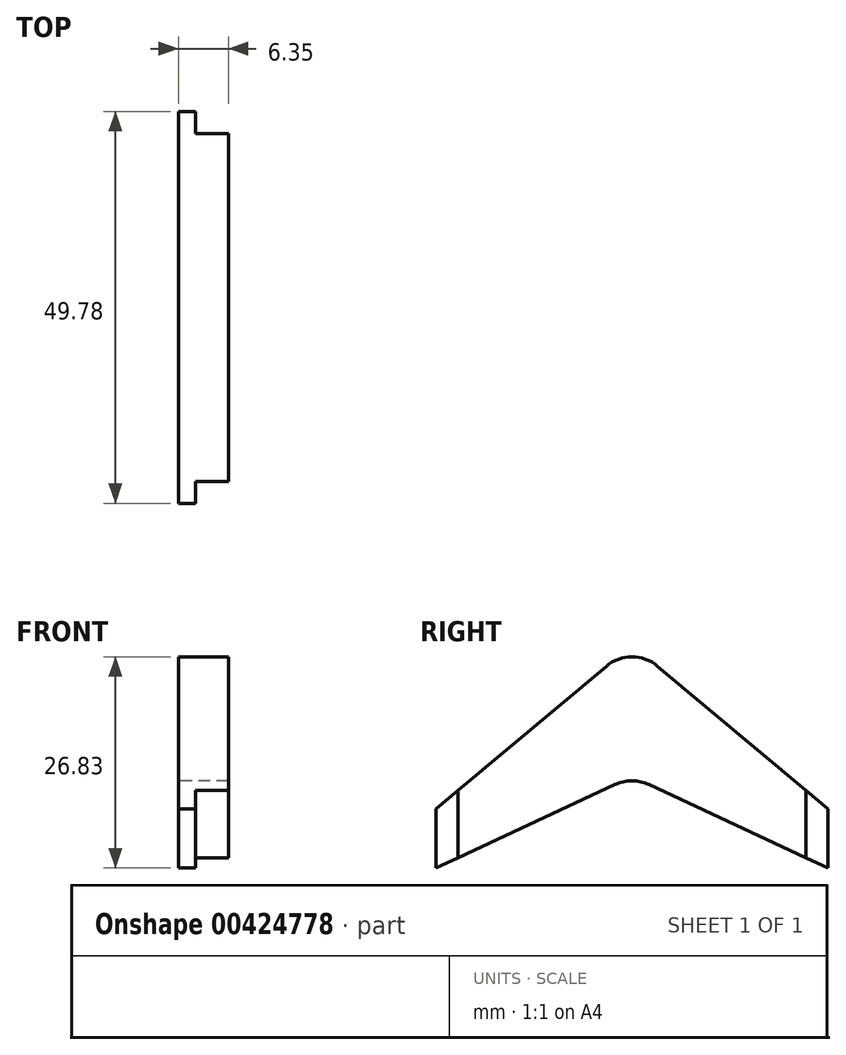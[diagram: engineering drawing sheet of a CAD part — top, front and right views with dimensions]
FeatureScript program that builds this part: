
annotation { "Feature Type Name" : "Feature", "Feature Type Description" : "" }
export const myFeature = defineFeature(function(context is Context, id is Id, definition is map)
    precondition{}
    {
        {
            var Q0;
            Q0=qCreatedBy(makeId("Right.planeOp"),FACE);
            var sketch = newSketch(context, id + "F0", { "sketchPlane" : qUnion([Q0])});
            skArc(sketch, "E0", {"start": v(3.27, 14.56) * mm, "mid": v(1.74, 15.44) * mm, "end": v(0, 15.75) * mm});
            skLineSegment(sketch, "E1", {"start": v(3.27, 14.56) * mm, "end": v(24.9, -3.59) * mm});
            skLineSegment(sketch, "E2", {"start": v(24.9, -3.59) * mm, "end": v(24.9, -11.08) * mm});
            skLineSegment(sketch, "E3", {"start": v(24.9, -11.08) * mm, "end": v(2.15, -0.48) * mm});
            skArc(sketch, "E4", {"start": v(2.15, -0.48) * mm, "mid": v(1.1, -0.12) * mm, "end": v(0, 0) * mm});
            skArc(sketch, "E5.MirrorCS", {"start": v(-2.15, -0.48) * mm, "mid": v(-1.1, -0.12) * mm, "end": v(0, 0) * mm});
            skLineSegment(sketch, "E6.MirrorCS", {"start": v(-24.9, -11.08) * mm, "end": v(-2.15, -0.48) * mm});
            skLineSegment(sketch, "E7.MirrorCS", {"start": v(-24.9, -3.59) * mm, "end": v(-24.9, -11.08) * mm});
            skLineSegment(sketch, "E8.MirrorCS", {"start": v(-3.27, 14.56) * mm, "end": v(-24.9, -3.59) * mm});
            skArc(sketch, "E9.MirrorCS", {"start": v(-3.27, 14.56) * mm, "mid": v(-1.74, 15.44) * mm, "end": v(0, 15.75) * mm});
            skSolve(sketch);
        }
        {
            var Q0;
            Q0=makeQuery(id+"F0.imprint","IMPRINT",FACE,{"disambiguationData":[TD([[makeQuery(id+"F0.imprint","IMPRINT",EDGE,{"derivedFrom":sQuery(id+"F0.wireOp",EDGE,"E0")}),1.0]])]});
            extrude(context, id + "F1", {"entities" : qUnion([Q0]), "depth" : 6.35 * mm});
        }
        {
            var Q0;
            Q0=makeQuery(id+"F1.opExtrude","CAP_FACE",FACE,{"disambiguationData":[OSD([sQuery(id+"F0.wireOp",EDGE,"E0"),sQuery(id+"F0.wireOp",EDGE,"E1"),sQuery(id+"F0.wireOp",EDGE,"E2"),sQuery(id+"F0.wireOp",EDGE,"E3"),sQuery(id+"F0.wireOp",EDGE,"E4"),sQuery(id+"F0.wireOp",EDGE,"E5.MirrorCS"),sQuery(id+"F0.wireOp",EDGE,"E6.MirrorCS"),sQuery(id+"F0.wireOp",EDGE,"E7.MirrorCS"),sQuery(id+"F0.wireOp",EDGE,"E8.MirrorCS"),sQuery(id+"F0.wireOp",EDGE,"E9.MirrorCS")])],"isStart":false});
            var sketch = newSketch(context, id + "F2", { "sketchPlane" : qUnion([Q0])});
            skLineSegment(sketch, "E10", {"start": v(24.9, -11.08) * mm, "end": v(24.9, -3.59) * mm});
            skLineSegment(sketch, "E11", {"start": v(24.9, -3.59) * mm, "end": v(22.1, -1.24) * mm});
            skLineSegment(sketch, "E12", {"start": v(22.1, -1.24) * mm, "end": v(22.1, -9.78) * mm});
            skLineSegment(sketch, "E13", {"start": v(22.1, -9.78) * mm, "end": v(24.9, -11.08) * mm});
            skLineSegment(sketch, "E14.MirrorCS", {"start": v(-22.1, -1.24) * mm, "end": v(-22.1, -9.78) * mm});
            skLineSegment(sketch, "E15.MirrorCS", {"start": v(-24.9, -3.59) * mm, "end": v(-22.1, -1.24) * mm});
            skLineSegment(sketch, "E16.MirrorCS", {"start": v(-24.9, -11.08) * mm, "end": v(-24.9, -3.59) * mm});
            skLineSegment(sketch, "E17.MirrorCS", {"start": v(-22.1, -9.78) * mm, "end": v(-24.9, -11.08) * mm});
            skSolve(sketch);
        }
        {
            var Q0;
            Q0=qSketchRegion(id+"F2",true);
            extrude(context, id + "F3", {"entities" : qUnion([Q0]), "operationType" : NewBodyOperationType.REMOVE, "oppositeDirection" : true, "depth" : 4.2 * mm});
        }
    });
